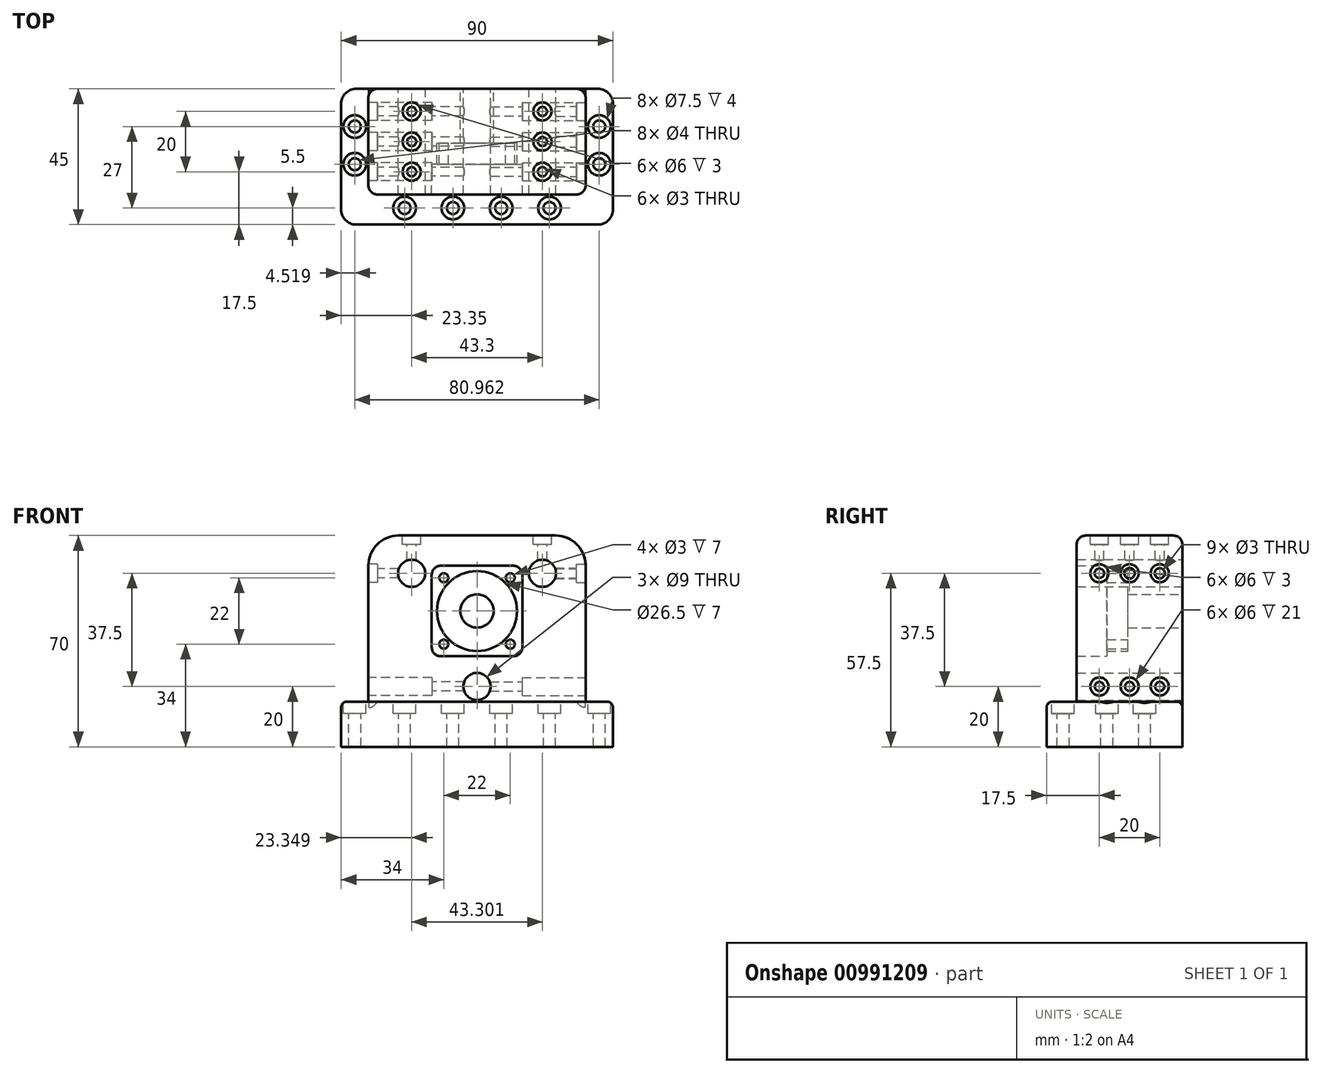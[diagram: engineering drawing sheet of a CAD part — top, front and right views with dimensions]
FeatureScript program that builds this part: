
annotation { "Feature Type Name" : "Feature", "Feature Type Description" : "" }
export const myFeature = defineFeature(function(context is Context, id is Id, definition is map)
    precondition{}
    {
        {
            var Q0;
            Q0=qCreatedBy(makeId("Front.planeOp"),FACE);
            var sketch = newSketch(context, id + "F0", { "sketchPlane" : qUnion([Q0])});
            skCircle(sketch, "E0", {"center": v(0, 0) * mm, "radius": 25 * mm, "construction": true});
            skLineSegment(sketch, "E1.0", {"start": v(0, -25) * mm, "end": v(-21.65, 12.5) * mm, "construction": true});
            skLineSegment(sketch, "E1.1", {"start": v(-21.65, 12.5) * mm, "end": v(21.65, 12.5) * mm, "construction": true});
            skLineSegment(sketch, "E1.2", {"start": v(21.65, 12.5) * mm, "end": v(0, -25) * mm, "construction": true});
            skCircle(sketch, "E2", {"center": v(21.65, 12.5) * mm, "radius": 4.5 * mm});
            skCircle(sketch, "E3", {"center": v(-21.65, 12.5) * mm, "radius": 4.5 * mm});
            skCircle(sketch, "E4", {"center": v(0, -25) * mm, "radius": 4.5 * mm});
            skPoint(sketch, "E5.cCircle.perimeterSnap0", {"position": v(0, 12.5) * mm});
            skLineSegment(sketch, "E5.0", {"start": v(-25.98, 25) * mm, "end": v(25.98, 25) * mm});
            skLineSegment(sketch, "E5.1", {"start": v(34.64, 10) * mm, "end": v(8.66, -35) * mm, "construction": true});
            skLineSegment(sketch, "E5.2", {"start": v(-8.66, -35) * mm, "end": v(-34.64, 10) * mm, "construction": true});
            skPoint(sketch, "E5.0.midPoint.positionSnap0", {"position": v(0, 12.5) * mm});
            skArc(sketch, "E6.filletArc", {"start": v(-25.98, 25) * mm, "mid": v(-34.64, 20) * mm, "end": v(-34.64, 10) * mm});
            skArc(sketch, "E7.filletArc", {"start": v(34.64, 10) * mm, "mid": v(34.64, 20) * mm, "end": v(25.98, 25) * mm});
            skArc(sketch, "E8.filletArc", {"start": v(-8.66, -35) * mm, "mid": v(0, -40) * mm, "end": v(8.66, -35) * mm, "construction": true});
            skLineSegment(sketch, "E9", {"start": v(35.98, 15) * mm, "end": v(35.98, -45) * mm});
            skCircle(sketch, "E10", {"center": v(0, 0) * mm, "radius": 5.5 * mm});
            skLineSegment(sketch, "E11", {"start": v(-35.98, 15) * mm, "end": v(-35.98, -45) * mm});
            skLineSegment(sketch, "E12", {"start": v(-35.98, -45) * mm, "end": v(35.98, -45) * mm});
            skLineSegment(sketch, "E13", {"start": v(-21.65, 12.5) * mm, "end": v(-35.98, 12.5) * mm, "construction": true});
            skLineSegment(sketch, "E14", {"start": v(21.65, 12.5) * mm, "end": v(35.98, 12.5) * mm, "construction": true});
            skLineSegment(sketch, "E15", {"start": v(0, -25) * mm, "end": v(35.98, -25) * mm, "construction": true});
            skLineSegment(sketch, "E16", {"start": v(0, -25) * mm, "end": v(-35.98, -25) * mm, "construction": true});
            skLineSegment(sketch, "E17", {"start": v(21.65, 12.5) * mm, "end": v(21.65, 25) * mm, "construction": true});
            skLineSegment(sketch, "E18", {"start": v(-21.65, 12.5) * mm, "end": v(-21.65, 25) * mm, "construction": true});
            skSolve(sketch);
        }
        {
            var Q0;
            Q0=qSketchRegion(id+"F0",true);
            extrude(context, id + "F1", {"entities" : qUnion([Q0]), "depth" : 18 * mm, "offsetDistance" : 25 * mm});
        }
        {
            var Q0;
            Q0=makeQuery(id+"F1.opExtrude","CAP_FACE",FACE,{"disambiguationData":[OSD([sQuery(id+"F0.wireOp",EDGE,"E2"),sQuery(id+"F0.wireOp",EDGE,"E3"),sQuery(id+"F0.wireOp",EDGE,"E4"),sQuery(id+"F0.wireOp",EDGE,"E5.0"),sQuery(id+"F0.wireOp",EDGE,"E6.filletArc"),sQuery(id+"F0.wireOp",EDGE,"E7.filletArc"),sQuery(id+"F0.wireOp",EDGE,"E9"),sQuery(id+"F0.wireOp",EDGE,"E10"),sQuery(id+"F0.wireOp",EDGE,"E11"),sQuery(id+"F0.wireOp",EDGE,"E12")])],"isStart":false});
            var sketch = newSketch(context, id + "F2", { "sketchPlane" : qUnion([Q0])});
            skCircle(sketch, "E19", {"center": v(0, 0) * mm, "radius": 13.25 * mm});
            skPoint(sketch, "E20.0.midPoint", {"position": v(0, 13.25) * mm});
            skLineSegment(sketch, "E21.bottom", {"start": v(11, 11) * mm, "end": v(-11, 11) * mm});
            skLineSegment(sketch, "E21.top", {"start": v(11, -11) * mm, "end": v(-11, -11) * mm});
            skLineSegment(sketch, "E21.left", {"start": v(11, 11) * mm, "end": v(11, -11) * mm});
            skLineSegment(sketch, "E21.right", {"start": v(-11, 11) * mm, "end": v(-11, -11) * mm});
            skCircle(sketch, "E22", {"center": v(11, 11) * mm, "radius": 1.5 * mm});
            skCircle(sketch, "E23", {"center": v(-11, 11) * mm, "radius": 1.5 * mm});
            skCircle(sketch, "E24", {"center": v(-11, -11) * mm, "radius": 1.5 * mm});
            skCircle(sketch, "E25", {"center": v(11, -11) * mm, "radius": 1.5 * mm});
            skSolve(sketch);
        }
        {
            var Q0;
            {var subQ0=sQuery(id+"F2.wireOp",EDGE,"E20.0");var subQ1=sQuery(id+"F2.wireOp",EDGE,"E19");var subQ2=makeQuery(id+"F2.imprint","INTERSECT",VERTEX,{"derivedFrom":[subQ1,subQ0]});Q0=makeQuery(id+"F2.imprint","IMPRINT",FACE,{"disambiguationData":[TD([[makeQuery(id+"F2.imprint","IMPRINT",EDGE,{"disambiguationData":[TD([[subQ2,1.0]])],"derivedFrom":subQ1}),-1.0]])]});}
            var Q1;
            {var subQ0=sQuery(id+"F2.wireOp",EDGE,"E20.0");var subQ1=sQuery(id+"F2.wireOp",EDGE,"E19");var subQ2=makeQuery(id+"F2.imprint","INTERSECT",VERTEX,{"derivedFrom":[subQ1,subQ0]});Q1=makeQuery(id+"F2.imprint","IMPRINT",FACE,{"disambiguationData":[TD([[makeQuery(id+"F2.imprint","IMPRINT",EDGE,{"disambiguationData":[TD([[subQ2,-1.0]])],"derivedFrom":subQ1}),-1.0]])]});}
            var Q2;
            {var subQ0=sQuery(id+"F2.wireOp",EDGE,"E20.3");var subQ1=sQuery(id+"F2.wireOp",EDGE,"E19");var subQ2=makeQuery(id+"F2.imprint","INTERSECT",VERTEX,{"derivedFrom":[subQ1,subQ0]});Q2=makeQuery(id+"F2.imprint","IMPRINT",FACE,{"disambiguationData":[TD([[makeQuery(id+"F2.imprint","IMPRINT",EDGE,{"disambiguationData":[TD([[subQ2,-1.0]])],"derivedFrom":subQ1}),-1.0]])]});}
            var Q3;
            {var subQ0=sQuery(id+"F2.wireOp",EDGE,"E20.1");var subQ1=sQuery(id+"F2.wireOp",EDGE,"E19");var subQ2=makeQuery(id+"F2.imprint","INTERSECT",VERTEX,{"derivedFrom":[subQ1,subQ0]});Q3=makeQuery(id+"F2.imprint","IMPRINT",FACE,{"disambiguationData":[TD([[makeQuery(id+"F2.imprint","IMPRINT",EDGE,{"disambiguationData":[TD([[subQ2,1.0]])],"derivedFrom":subQ1}),-1.0]])]});}
            var Q4;
            Q4=makeQuery(id+"F2.imprint","IMPRINT",FACE,{"disambiguationData":[TD([[makeQuery(id+"F2.imprint","IMPRINT",EDGE,{"derivedFrom":makeQuery(id+"F1.opExtrude","CAP_EDGE",EDGE,{"disambiguationData":[OSD([sQuery(id+"F0.wireOp",EDGE,"E2")])],"isStart":false})}),-1.0]])]});
            var Q5;
            {var subQ0=sQuery(id+"F2.wireOp",EDGE,"E21.bottom");var subQ1=sQuery(id+"F2.wireOp",EDGE,"E19");var subQ2=makeQuery(id+"F2.imprint","INTERSECT",VERTEX,{"disambiguationData":[OD(1.0)],"derivedFrom":[subQ1,subQ0]});Q5=makeQuery(id+"F2.imprint","IMPRINT",FACE,{"disambiguationData":[TD([[makeQuery(id+"F2.imprint","IMPRINT",EDGE,{"disambiguationData":[TD([[subQ2,-1.0]])],"derivedFrom":subQ1}),-1.0]])]});}
            var Q6;
            {var subQ0=sQuery(id+"F2.wireOp",EDGE,"E21.bottom");var subQ1=sQuery(id+"F2.wireOp",EDGE,"E19");var subQ2=makeQuery(id+"F2.imprint","INTERSECT",VERTEX,{"disambiguationData":[OD(0.0)],"derivedFrom":[subQ1,subQ0]});Q6=makeQuery(id+"F2.imprint","IMPRINT",FACE,{"disambiguationData":[TD([[makeQuery(id+"F2.imprint","IMPRINT",EDGE,{"disambiguationData":[TD([[subQ2,1.0]])],"derivedFrom":subQ1}),-1.0]])]});}
            var Q7;
            {var subQ0=sQuery(id+"F2.wireOp",EDGE,"E21.top");var subQ1=sQuery(id+"F2.wireOp",EDGE,"E19");var subQ2=makeQuery(id+"F2.imprint","INTERSECT",VERTEX,{"disambiguationData":[OD(1.0)],"derivedFrom":[subQ1,subQ0]});Q7=makeQuery(id+"F2.imprint","IMPRINT",FACE,{"disambiguationData":[TD([[makeQuery(id+"F2.imprint","IMPRINT",EDGE,{"disambiguationData":[TD([[subQ2,-1.0]])],"derivedFrom":subQ1}),-1.0]])]});}
            var Q8;
            {var subQ0=sQuery(id+"F2.wireOp",EDGE,"E21.right");var subQ1=sQuery(id+"F2.wireOp",EDGE,"E19");var subQ2=makeQuery(id+"F2.imprint","INTERSECT",VERTEX,{"disambiguationData":[OD(1.0)],"derivedFrom":[subQ1,subQ0]});Q8=makeQuery(id+"F2.imprint","IMPRINT",FACE,{"disambiguationData":[TD([[makeQuery(id+"F2.imprint","IMPRINT",EDGE,{"disambiguationData":[TD([[subQ2,-1.0]])],"derivedFrom":subQ1}),-1.0]])]});}
            extrude(context, id + "F3", {"entities" : qUnion([Q0, Q1, Q2, Q3, Q4, Q5, Q6, Q7, Q8]), "operationType" : NewBodyOperationType.ADD, "depth" : 7 * mm, "offsetDistance" : 25 * mm});
        }
        {
            var Q0;
            Q0=makeQuery(id+"F3.opExtrude","CAP_FACE",FACE,{"disambiguationData":[OSD([sQuery(id+"F0.wireOp",EDGE,"E2"),sQuery(id+"F0.wireOp",EDGE,"E3"),sQuery(id+"F0.wireOp",EDGE,"E4"),sQuery(id+"F0.wireOp",EDGE,"E5.0"),sQuery(id+"F0.wireOp",EDGE,"E6.filletArc"),sQuery(id+"F0.wireOp",EDGE,"E7.filletArc"),sQuery(id+"F0.wireOp",EDGE,"E9"),sQuery(id+"F0.wireOp",EDGE,"E11"),sQuery(id+"F0.wireOp",EDGE,"E12"),sQuery(id+"F2.wireOp",EDGE,"E19"),sQuery(id+"F2.wireOp",EDGE,"eFj7zF5P-7EVq-kD0F-ThRH-6Hop9WIGIFQv"),sQuery(id+"F2.wireOp",EDGE,"omm04afh-Djjw-QQMO-E9Vr-uDkzuJGtbU2r"),sQuery(id+"F2.wireOp",EDGE,"DAAaBMiw-Czrf-eRyD-MXHk-odGZbSsKrrbm"),sQuery(id+"F2.wireOp",EDGE,"t53pX8GN-pWrL-uYky-B8yh-KqMqTwP7CCYq")])],"isStart":false});
            var sketch = newSketch(context, id + "F4", { "sketchPlane" : qUnion([Q0])});
            skLineSegment(sketch, "E26.bottom", {"start": v(-12, 15) * mm, "end": v(12, 15) * mm});
            skLineSegment(sketch, "E26.top", {"start": v(-12, -15) * mm, "end": v(12, -15) * mm});
            skLineSegment(sketch, "E26.left", {"start": v(-15, 12) * mm, "end": v(-15, -12) * mm});
            skLineSegment(sketch, "E26.right", {"start": v(15, 12) * mm, "end": v(15, -12) * mm});
            skPoint(sketch, "E26.middle", {"position": v(0, 0) * mm});
            skPoint(sketch, "E27.visualSharp", {"position": v(-15, 15) * mm});
            skArc(sketch, "E27.filletArc", {"start": v(-12, 15) * mm, "mid": v(-14.12, 14.12) * mm, "end": v(-15, 12) * mm});
            skPoint(sketch, "E28.visualSharp", {"position": v(15, 15) * mm});
            skArc(sketch, "E28.filletArc", {"start": v(15, 12) * mm, "mid": v(14.12, 14.12) * mm, "end": v(12, 15) * mm});
            skPoint(sketch, "E29.visualSharp", {"position": v(-15, -15) * mm});
            skArc(sketch, "E29.filletArc", {"start": v(-15, -12) * mm, "mid": v(-14.12, -14.12) * mm, "end": v(-12, -15) * mm});
            skPoint(sketch, "E30.visualSharp", {"position": v(15, -15) * mm});
            skArc(sketch, "E30.filletArc", {"start": v(12, -15) * mm, "mid": v(14.12, -14.12) * mm, "end": v(15, -12) * mm});
            skSolve(sketch);
        }
        {
            var Q0;
            Q0=makeQuery(id+"F4.imprint","IMPRINT",FACE,{"disambiguationData":[TD([[makeQuery(id+"F4.imprint","IMPRINT",EDGE,{"derivedFrom":sQuery(id+"F4.wireOp",EDGE,"E26.bottom")}),1.0]])]});
            extrude(context, id + "F5", {"entities" : qUnion([Q0]), "operationType" : NewBodyOperationType.ADD, "depth" : 10 * mm, "offsetDistance" : 25 * mm});
        }
        {
            var Q0;
            {var subQ0=sQuery(id+"F0.wireOp",EDGE,"E9");Q0=makeQuery(id+"F5.boolean.opBoolean","MERGE",FACE,{"derivedFrom":[makeQuery(id+"F3.boolean.opBoolean","MERGE",FACE,{"derivedFrom":[makeQuery(id+"F1.opExtrude","SWEPT_FACE",FACE,{"disambiguationData":[OSD([subQ0])]}),makeQuery(id+"F3.opExtrude","SWEPT_FACE",FACE,{"disambiguationData":[OSD([subQ0])]})]}),makeQuery(id+"F5.opExtrude","SWEPT_FACE",FACE,{"disambiguationData":[OSD([subQ0])]})]});}
            var sketch = newSketch(context, id + "F6", { "sketchPlane" : qUnion([Q0])});
            skLineSegment(sketch, "E31", {"start": v(-17.5, 15) * mm, "end": v(-17.5, 0) * mm, "construction": true});
            skLineSegment(sketch, "E32", {"start": v(-27.5, 15) * mm, "end": v(-27.5, 0) * mm, "construction": true});
            skLineSegment(sketch, "E33", {"start": v(-7.5, 15) * mm, "end": v(-7.5, 0) * mm, "construction": true});
            skLineSegment(sketch, "E34", {"start": v(0, 12.5) * mm, "end": v(-35, 12.5) * mm, "construction": true});
            skCircle(sketch, "E35", {"center": v(-27.5, 12.5) * mm, "radius": 3 * mm});
            skCircle(sketch, "E36", {"center": v(-17.5, 12.5) * mm, "radius": 3 * mm});
            skCircle(sketch, "E37", {"center": v(-7.5, 12.5) * mm, "radius": 3 * mm});
            skCircle(sketch, "E38", {"center": v(-27.5, 12.5) * mm, "radius": 1.57 * mm});
            skCircle(sketch, "E39", {"center": v(-17.5, 12.5) * mm, "radius": 1.74 * mm});
            skCircle(sketch, "E40", {"center": v(-7.5, 12.5) * mm, "radius": 1.68 * mm});
            skLineSegment(sketch, "E41", {"start": v(-27.5, 0) * mm, "end": v(-27.5, -45) * mm, "construction": true});
            skLineSegment(sketch, "E42", {"start": v(-17.5, 0) * mm, "end": v(-17.5, -45) * mm, "construction": true});
            skLineSegment(sketch, "E43", {"start": v(-7.5, 0) * mm, "end": v(-7.5, -45) * mm, "construction": true});
            skLineSegment(sketch, "E44", {"start": v(0, -25) * mm, "end": v(-35, -25) * mm, "construction": true});
            skCircle(sketch, "E45", {"center": v(-27.5, -25) * mm, "radius": 3 * mm});
            skCircle(sketch, "E46", {"center": v(-17.5, -25) * mm, "radius": 3 * mm});
            skCircle(sketch, "E47", {"center": v(-7.5, -25) * mm, "radius": 3 * mm});
            skCircle(sketch, "E48", {"center": v(-27.5, -25) * mm, "radius": 1.5 * mm});
            skCircle(sketch, "E49", {"center": v(-17.5, -25) * mm, "radius": 1.5 * mm});
            skCircle(sketch, "E50", {"center": v(-7.5, -25) * mm, "radius": 1.5 * mm});
            skSolve(sketch);
        }
        {
            var Q0;
            Q0=makeQuery(id+"F6.imprint","IMPRINT",FACE,{"disambiguationData":[TD([[makeQuery(id+"F6.imprint","IMPRINT",EDGE,{"derivedFrom":sQuery(id+"F6.wireOp",EDGE,"E38")}),1.0]])]});
            var Q1;
            Q1=makeQuery(id+"F6.imprint","IMPRINT",FACE,{"disambiguationData":[TD([[makeQuery(id+"F6.imprint","IMPRINT",EDGE,{"derivedFrom":sQuery(id+"F6.wireOp",EDGE,"E39")}),1.0]])]});
            var Q2;
            Q2=makeQuery(id+"F6.imprint","IMPRINT",FACE,{"disambiguationData":[TD([[makeQuery(id+"F6.imprint","IMPRINT",EDGE,{"derivedFrom":sQuery(id+"F6.wireOp",EDGE,"E40")}),1.0]])]});
            var Q3;
            {var subQ0=sQuery(id+"F6.wireOp",EDGE,"E35");var subQ1=sQuery(id+"F0.wireOp",EDGE,"E9");var subQ2=sQuery(id+"F0.wireOp",EDGE,"E7.filletArc");var subQ3=makeQuery(id+"F5.boolean.opBoolean","MERGE",EDGE,{"derivedFrom":[makeQuery(id+"F3.boolean.opBoolean","MERGE",EDGE,{"derivedFrom":[makeQuery(id+"F1.opExtrude","SWEPT_EDGE",EDGE,{"disambiguationData":[OSD([subQ2,subQ1])]}),makeQuery(id+"F3.opExtrude","SWEPT_EDGE",EDGE,{"disambiguationData":[OSD([subQ2,subQ1])]})]}),makeQuery(id+"F5.opExtrude","SWEPT_EDGE",EDGE,{"disambiguationData":[OSD([subQ2,subQ1])]})]});var subQ4=makeQuery(id+"F6.imprint","INTERSECT",VERTEX,{"disambiguationData":[OD(0.0)],"derivedFrom":[subQ3,subQ0]});Q3=makeQuery(id+"F6.imprint","IMPRINT",FACE,{"disambiguationData":[TD([[makeQuery(id+"F6.imprint","IMPRINT",EDGE,{"disambiguationData":[TD([[subQ4,1.0]])],"derivedFrom":subQ0}),1.0]])]});}
            var Q4;
            {var subQ0=sQuery(id+"F6.wireOp",EDGE,"E36");var subQ1=sQuery(id+"F0.wireOp",EDGE,"E9");var subQ2=sQuery(id+"F0.wireOp",EDGE,"E7.filletArc");var subQ3=makeQuery(id+"F5.boolean.opBoolean","MERGE",EDGE,{"derivedFrom":[makeQuery(id+"F3.boolean.opBoolean","MERGE",EDGE,{"derivedFrom":[makeQuery(id+"F1.opExtrude","SWEPT_EDGE",EDGE,{"disambiguationData":[OSD([subQ2,subQ1])]}),makeQuery(id+"F3.opExtrude","SWEPT_EDGE",EDGE,{"disambiguationData":[OSD([subQ2,subQ1])]})]}),makeQuery(id+"F5.opExtrude","SWEPT_EDGE",EDGE,{"disambiguationData":[OSD([subQ2,subQ1])]})]});var subQ4=makeQuery(id+"F6.imprint","INTERSECT",VERTEX,{"disambiguationData":[OD(0.0)],"derivedFrom":[subQ3,subQ0]});Q4=makeQuery(id+"F6.imprint","IMPRINT",FACE,{"disambiguationData":[TD([[makeQuery(id+"F6.imprint","IMPRINT",EDGE,{"disambiguationData":[TD([[subQ4,1.0]])],"derivedFrom":subQ0}),1.0]])]});}
            var Q5;
            {var subQ0=sQuery(id+"F6.wireOp",EDGE,"E37");var subQ1=sQuery(id+"F0.wireOp",EDGE,"E9");var subQ2=sQuery(id+"F0.wireOp",EDGE,"E7.filletArc");var subQ3=makeQuery(id+"F5.boolean.opBoolean","MERGE",EDGE,{"derivedFrom":[makeQuery(id+"F3.boolean.opBoolean","MERGE",EDGE,{"derivedFrom":[makeQuery(id+"F1.opExtrude","SWEPT_EDGE",EDGE,{"disambiguationData":[OSD([subQ2,subQ1])]}),makeQuery(id+"F3.opExtrude","SWEPT_EDGE",EDGE,{"disambiguationData":[OSD([subQ2,subQ1])]})]}),makeQuery(id+"F5.opExtrude","SWEPT_EDGE",EDGE,{"disambiguationData":[OSD([subQ2,subQ1])]})]});var subQ4=makeQuery(id+"F6.imprint","INTERSECT",VERTEX,{"disambiguationData":[OD(0.0)],"derivedFrom":[subQ3,subQ0]});Q5=makeQuery(id+"F6.imprint","IMPRINT",FACE,{"disambiguationData":[TD([[makeQuery(id+"F6.imprint","IMPRINT",EDGE,{"disambiguationData":[TD([[subQ4,-1.0]])],"derivedFrom":subQ0}),1.0]])]});}
            var Q6;
            Q6=makeQuery(id+"F6.imprint","IMPRINT",FACE,{"disambiguationData":[TD([[makeQuery(id+"F6.imprint","IMPRINT",EDGE,{"derivedFrom":sQuery(id+"F6.wireOp",EDGE,"E38")}),-1.0]])]});
            var Q7;
            Q7=makeQuery(id+"F6.imprint","IMPRINT",FACE,{"disambiguationData":[TD([[makeQuery(id+"F6.imprint","IMPRINT",EDGE,{"derivedFrom":sQuery(id+"F6.wireOp",EDGE,"E39")}),-1.0]])]});
            var Q8;
            Q8=makeQuery(id+"F6.imprint","IMPRINT",FACE,{"disambiguationData":[TD([[makeQuery(id+"F6.imprint","IMPRINT",EDGE,{"derivedFrom":sQuery(id+"F6.wireOp",EDGE,"E40")}),-1.0]])]});
            extrude(context, id + "F7", {"entities" : qUnion([Q0, Q1, Q2, Q3, Q4, Q5, Q6, Q7, Q8]), "operationType" : NewBodyOperationType.REMOVE, "oppositeDirection" : true, "depth" : 3 * mm, "offsetDistance" : 25 * mm});
        }
        {
            var Q0;
            Q0=makeQuery(id+"F6.imprint","IMPRINT",FACE,{"disambiguationData":[TD([[makeQuery(id+"F6.imprint","IMPRINT",EDGE,{"derivedFrom":sQuery(id+"F6.wireOp",EDGE,"E38")}),1.0]])]});
            var Q1;
            Q1=makeQuery(id+"F6.imprint","IMPRINT",FACE,{"disambiguationData":[TD([[makeQuery(id+"F6.imprint","IMPRINT",EDGE,{"derivedFrom":sQuery(id+"F6.wireOp",EDGE,"E39")}),1.0]])]});
            var Q2;
            Q2=makeQuery(id+"F6.imprint","IMPRINT",FACE,{"disambiguationData":[TD([[makeQuery(id+"F6.imprint","IMPRINT",EDGE,{"derivedFrom":sQuery(id+"F6.wireOp",EDGE,"E40")}),1.0]])]});
            extrude(context, id + "F8", {"entities" : qUnion([Q0, Q1, Q2]), "operationType" : NewBodyOperationType.REMOVE, "oppositeDirection" : true, "depth" : 11 * mm, "offsetDistance" : 25 * mm});
        }
        {
            var Q0;
            {var subQ0=sQuery(id+"F0.wireOp",EDGE,"E11");Q0=makeQuery(id+"F5.boolean.opBoolean","MERGE",FACE,{"derivedFrom":[makeQuery(id+"F3.boolean.opBoolean","MERGE",FACE,{"derivedFrom":[makeQuery(id+"F1.opExtrude","SWEPT_FACE",FACE,{"disambiguationData":[OSD([subQ0])]}),makeQuery(id+"F3.opExtrude","SWEPT_FACE",FACE,{"disambiguationData":[OSD([subQ0])]})]}),makeQuery(id+"F5.opExtrude","SWEPT_FACE",FACE,{"disambiguationData":[OSD([subQ0])]})]});}
            var sketch = newSketch(context, id + "F9", { "sketchPlane" : qUnion([Q0])});
            skLineSegment(sketch, "E51", {"start": v(17.5, 15) * mm, "end": v(17.5, 0) * mm, "construction": true});
            skLineSegment(sketch, "E52", {"start": v(27.5, 15) * mm, "end": v(27.5, 0) * mm, "construction": true});
            skLineSegment(sketch, "E53", {"start": v(7.5, 15) * mm, "end": v(7.5, 0) * mm, "construction": true});
            skLineSegment(sketch, "E54", {"start": v(0, 12.5) * mm, "end": v(35, 12.5) * mm, "construction": true});
            skCircle(sketch, "E55", {"center": v(7.5, 12.5) * mm, "radius": 3 * mm});
            skCircle(sketch, "E56", {"center": v(17.5, 12.5) * mm, "radius": 3 * mm});
            skCircle(sketch, "E57", {"center": v(27.5, 12.5) * mm, "radius": 3 * mm});
            skCircle(sketch, "E58", {"center": v(27.5, 12.5) * mm, "radius": 1.5 * mm});
            skCircle(sketch, "E59", {"center": v(17.5, 12.5) * mm, "radius": 1.5 * mm});
            skCircle(sketch, "E60", {"center": v(7.5, 12.5) * mm, "radius": 1.5 * mm});
            skLineSegment(sketch, "E61", {"start": v(7.5, 0) * mm, "end": v(7.5, -45) * mm, "construction": true});
            skLineSegment(sketch, "E62", {"start": v(17.5, 0) * mm, "end": v(17.5, -45) * mm, "construction": true});
            skLineSegment(sketch, "E63", {"start": v(27.5, 0) * mm, "end": v(27.5, -45) * mm, "construction": true});
            skLineSegment(sketch, "E64", {"start": v(0, -25) * mm, "end": v(35, -25) * mm, "construction": true});
            skCircle(sketch, "E65", {"center": v(7.5, -25) * mm, "radius": 3 * mm});
            skCircle(sketch, "E66", {"center": v(17.5, -25) * mm, "radius": 3 * mm});
            skCircle(sketch, "E67", {"center": v(27.5, -25) * mm, "radius": 3 * mm});
            skCircle(sketch, "E68", {"center": v(7.5, -25) * mm, "radius": 1.5 * mm});
            skCircle(sketch, "E69", {"center": v(17.5, -25) * mm, "radius": 1.5 * mm});
            skCircle(sketch, "E70", {"center": v(27.5, -25) * mm, "radius": 1.5 * mm});
            skSolve(sketch);
        }
        {
            var Q0;
            Q0=makeQuery(id+"F9.imprint","IMPRINT",FACE,{"disambiguationData":[TD([[makeQuery(id+"F9.imprint","IMPRINT",EDGE,{"derivedFrom":sQuery(id+"F9.wireOp",EDGE,"E60")}),-1.0]])]});
            var Q1;
            Q1=makeQuery(id+"F9.imprint","IMPRINT",FACE,{"disambiguationData":[TD([[makeQuery(id+"F9.imprint","IMPRINT",EDGE,{"derivedFrom":sQuery(id+"F9.wireOp",EDGE,"E60")}),1.0]])]});
            var Q2;
            Q2=makeQuery(id+"F9.imprint","IMPRINT",FACE,{"disambiguationData":[TD([[makeQuery(id+"F9.imprint","IMPRINT",EDGE,{"derivedFrom":sQuery(id+"F9.wireOp",EDGE,"E59")}),-1.0]])]});
            var Q3;
            {var subQ0=sQuery(id+"F9.wireOp",EDGE,"E56");var subQ1=sQuery(id+"F0.wireOp",EDGE,"E11");var subQ2=sQuery(id+"F0.wireOp",EDGE,"E6.filletArc");var subQ3=makeQuery(id+"F5.boolean.opBoolean","MERGE",EDGE,{"derivedFrom":[makeQuery(id+"F3.boolean.opBoolean","MERGE",EDGE,{"derivedFrom":[makeQuery(id+"F1.opExtrude","SWEPT_EDGE",EDGE,{"disambiguationData":[OSD([subQ2,subQ1])]}),makeQuery(id+"F3.opExtrude","SWEPT_EDGE",EDGE,{"disambiguationData":[OSD([subQ2,subQ1])]})]}),makeQuery(id+"F5.opExtrude","SWEPT_EDGE",EDGE,{"disambiguationData":[OSD([subQ2,subQ1])]})]});var subQ4=makeQuery(id+"F9.imprint","INTERSECT",VERTEX,{"disambiguationData":[OD(0.0)],"derivedFrom":[subQ3,subQ0]});Q3=makeQuery(id+"F9.imprint","IMPRINT",FACE,{"disambiguationData":[TD([[makeQuery(id+"F9.imprint","IMPRINT",EDGE,{"disambiguationData":[TD([[subQ4,1.0]])],"derivedFrom":subQ0}),1.0]])]});}
            var Q4;
            Q4=makeQuery(id+"F9.imprint","IMPRINT",FACE,{"disambiguationData":[TD([[makeQuery(id+"F9.imprint","IMPRINT",EDGE,{"derivedFrom":sQuery(id+"F9.wireOp",EDGE,"E59")}),1.0]])]});
            var Q5;
            Q5=makeQuery(id+"F9.imprint","IMPRINT",FACE,{"disambiguationData":[TD([[makeQuery(id+"F9.imprint","IMPRINT",EDGE,{"derivedFrom":sQuery(id+"F9.wireOp",EDGE,"E58")}),-1.0]])]});
            var Q6;
            {var subQ0=sQuery(id+"F9.wireOp",EDGE,"E57");var subQ1=sQuery(id+"F0.wireOp",EDGE,"E11");var subQ2=sQuery(id+"F0.wireOp",EDGE,"E6.filletArc");var subQ3=makeQuery(id+"F5.boolean.opBoolean","MERGE",EDGE,{"derivedFrom":[makeQuery(id+"F3.boolean.opBoolean","MERGE",EDGE,{"derivedFrom":[makeQuery(id+"F1.opExtrude","SWEPT_EDGE",EDGE,{"disambiguationData":[OSD([subQ2,subQ1])]}),makeQuery(id+"F3.opExtrude","SWEPT_EDGE",EDGE,{"disambiguationData":[OSD([subQ2,subQ1])]})]}),makeQuery(id+"F5.opExtrude","SWEPT_EDGE",EDGE,{"disambiguationData":[OSD([subQ2,subQ1])]})]});var subQ4=makeQuery(id+"F9.imprint","INTERSECT",VERTEX,{"disambiguationData":[OD(0.0)],"derivedFrom":[subQ3,subQ0]});Q6=makeQuery(id+"F9.imprint","IMPRINT",FACE,{"disambiguationData":[TD([[makeQuery(id+"F9.imprint","IMPRINT",EDGE,{"disambiguationData":[TD([[subQ4,-1.0]])],"derivedFrom":subQ0}),1.0]])]});}
            var Q7;
            Q7=makeQuery(id+"F9.imprint","IMPRINT",FACE,{"disambiguationData":[TD([[makeQuery(id+"F9.imprint","IMPRINT",EDGE,{"derivedFrom":sQuery(id+"F9.wireOp",EDGE,"E58")}),1.0]])]});
            var Q8;
            {var subQ0=sQuery(id+"F9.wireOp",EDGE,"E55");var subQ1=sQuery(id+"F0.wireOp",EDGE,"E11");var subQ2=sQuery(id+"F0.wireOp",EDGE,"E6.filletArc");var subQ3=makeQuery(id+"F5.boolean.opBoolean","MERGE",EDGE,{"derivedFrom":[makeQuery(id+"F3.boolean.opBoolean","MERGE",EDGE,{"derivedFrom":[makeQuery(id+"F1.opExtrude","SWEPT_EDGE",EDGE,{"disambiguationData":[OSD([subQ2,subQ1])]}),makeQuery(id+"F3.opExtrude","SWEPT_EDGE",EDGE,{"disambiguationData":[OSD([subQ2,subQ1])]})]}),makeQuery(id+"F5.opExtrude","SWEPT_EDGE",EDGE,{"disambiguationData":[OSD([subQ2,subQ1])]})]});var subQ4=makeQuery(id+"F9.imprint","INTERSECT",VERTEX,{"disambiguationData":[OD(0.0)],"derivedFrom":[subQ3,subQ0]});Q8=makeQuery(id+"F9.imprint","IMPRINT",FACE,{"disambiguationData":[TD([[makeQuery(id+"F9.imprint","IMPRINT",EDGE,{"disambiguationData":[TD([[subQ4,1.0]])],"derivedFrom":subQ0}),1.0]])]});}
            extrude(context, id + "F10", {"entities" : qUnion([Q0, Q1, Q2, Q3, Q4, Q5, Q6, Q7, Q8]), "operationType" : NewBodyOperationType.REMOVE, "oppositeDirection" : true, "depth" : 3 * mm, "offsetDistance" : 25 * mm});
        }
        {
            var Q0;
            Q0=makeQuery(id+"F9.imprint","IMPRINT",FACE,{"disambiguationData":[TD([[makeQuery(id+"F9.imprint","IMPRINT",EDGE,{"derivedFrom":sQuery(id+"F9.wireOp",EDGE,"E60")}),1.0]])]});
            var Q1;
            Q1=makeQuery(id+"F9.imprint","IMPRINT",FACE,{"disambiguationData":[TD([[makeQuery(id+"F9.imprint","IMPRINT",EDGE,{"derivedFrom":sQuery(id+"F9.wireOp",EDGE,"E59")}),1.0]])]});
            var Q2;
            Q2=makeQuery(id+"F9.imprint","IMPRINT",FACE,{"disambiguationData":[TD([[makeQuery(id+"F9.imprint","IMPRINT",EDGE,{"derivedFrom":sQuery(id+"F9.wireOp",EDGE,"E58")}),1.0]])]});
            extrude(context, id + "F11", {"entities" : qUnion([Q0, Q1, Q2]), "operationType" : NewBodyOperationType.REMOVE, "oppositeDirection" : true, "depth" : 11 * mm, "offsetDistance" : 25 * mm});
        }
        {
            var Q0;
            {var subQ0=sQuery(id+"F0.wireOp",EDGE,"E5.0");Q0=makeQuery(id+"F5.boolean.opBoolean","MERGE",FACE,{"derivedFrom":[makeQuery(id+"F3.boolean.opBoolean","MERGE",FACE,{"derivedFrom":[makeQuery(id+"F1.opExtrude","SWEPT_FACE",FACE,{"disambiguationData":[OSD([subQ0])]}),makeQuery(id+"F3.opExtrude","SWEPT_FACE",FACE,{"disambiguationData":[OSD([subQ0])]})]}),makeQuery(id+"F5.opExtrude","SWEPT_FACE",FACE,{"disambiguationData":[OSD([subQ0])]})]});}
            var sketch = newSketch(context, id + "F12", { "sketchPlane" : qUnion([Q0])});
            skLineSegment(sketch, "E71", {"start": v(-25.98, -17.5) * mm, "end": v(25.98, -17.5) * mm, "construction": true});
            skLineSegment(sketch, "E72", {"start": v(25.98, -7.5) * mm, "end": v(-25.98, -7.5) * mm, "construction": true});
            skLineSegment(sketch, "E73", {"start": v(25.98, -27.5) * mm, "end": v(-25.98, -27.5) * mm, "construction": true});
            skLineSegment(sketch, "E74", {"start": v(-21.65, 0) * mm, "end": v(-21.65, -35) * mm, "construction": true});
            skLineSegment(sketch, "E75", {"start": v(21.65, 0) * mm, "end": v(21.65, -35) * mm, "construction": true});
            skCircle(sketch, "E76", {"center": v(-21.65, -7.5) * mm, "radius": 3 * mm});
            skCircle(sketch, "E77", {"center": v(-21.65, -17.5) * mm, "radius": 3 * mm});
            skCircle(sketch, "E78", {"center": v(-21.65, -27.5) * mm, "radius": 3 * mm});
            skCircle(sketch, "E79", {"center": v(21.65, -7.5) * mm, "radius": 3 * mm});
            skCircle(sketch, "E80", {"center": v(21.65, -17.5) * mm, "radius": 3 * mm});
            skCircle(sketch, "E81", {"center": v(21.65, -27.5) * mm, "radius": 3 * mm});
            skCircle(sketch, "E82", {"center": v(-21.65, -7.5) * mm, "radius": 1.5 * mm});
            skCircle(sketch, "E83", {"center": v(-21.65, -17.5) * mm, "radius": 1.5 * mm});
            skCircle(sketch, "E84", {"center": v(-21.65, -27.5) * mm, "radius": 1.5 * mm});
            skCircle(sketch, "E85", {"center": v(21.65, -7.5) * mm, "radius": 1.5 * mm});
            skCircle(sketch, "E86", {"center": v(21.65, -17.5) * mm, "radius": 1.5 * mm});
            skCircle(sketch, "E87", {"center": v(21.65, -27.5) * mm, "radius": 1.5 * mm});
            skSolve(sketch);
        }
        {
            var Q0;
            Q0=makeQuery(id+"F12.imprint","IMPRINT",FACE,{"disambiguationData":[TD([[makeQuery(id+"F12.imprint","IMPRINT",EDGE,{"derivedFrom":sQuery(id+"F12.wireOp",EDGE,"E76")}),1.0]])]});
            var Q1;
            Q1=makeQuery(id+"F12.imprint","IMPRINT",FACE,{"disambiguationData":[TD([[makeQuery(id+"F12.imprint","IMPRINT",EDGE,{"derivedFrom":sQuery(id+"F12.wireOp",EDGE,"E77")}),1.0]])]});
            var Q2;
            Q2=makeQuery(id+"F12.imprint","IMPRINT",FACE,{"disambiguationData":[TD([[makeQuery(id+"F12.imprint","IMPRINT",EDGE,{"derivedFrom":sQuery(id+"F12.wireOp",EDGE,"E78")}),1.0]])]});
            var Q3;
            Q3=makeQuery(id+"F12.imprint","IMPRINT",FACE,{"disambiguationData":[TD([[makeQuery(id+"F12.imprint","IMPRINT",EDGE,{"derivedFrom":sQuery(id+"F12.wireOp",EDGE,"E79")}),1.0]])]});
            var Q4;
            Q4=makeQuery(id+"F12.imprint","IMPRINT",FACE,{"disambiguationData":[TD([[makeQuery(id+"F12.imprint","IMPRINT",EDGE,{"derivedFrom":sQuery(id+"F12.wireOp",EDGE,"E80")}),1.0]])]});
            var Q5;
            Q5=makeQuery(id+"F12.imprint","IMPRINT",FACE,{"disambiguationData":[TD([[makeQuery(id+"F12.imprint","IMPRINT",EDGE,{"derivedFrom":sQuery(id+"F12.wireOp",EDGE,"E81")}),1.0]])]});
            extrude(context, id + "F13", {"entities" : qUnion([Q0, Q1, Q2, Q3, Q4, Q5]), "operationType" : NewBodyOperationType.REMOVE, "oppositeDirection" : true, "depth" : 3 * mm, "offsetDistance" : 25 * mm});
        }
        {
            var Q0;
            Q0=makeQuery(id+"F12.imprint","IMPRINT",FACE,{"disambiguationData":[TD([[makeQuery(id+"F12.imprint","IMPRINT",EDGE,{"derivedFrom":sQuery(id+"F12.wireOp",EDGE,"E82")}),1.0]])]});
            var Q1;
            Q1=makeQuery(id+"F12.imprint","IMPRINT",FACE,{"disambiguationData":[TD([[makeQuery(id+"F12.imprint","IMPRINT",EDGE,{"derivedFrom":sQuery(id+"F12.wireOp",EDGE,"E83")}),1.0]])]});
            var Q2;
            Q2=makeQuery(id+"F12.imprint","IMPRINT",FACE,{"disambiguationData":[TD([[makeQuery(id+"F12.imprint","IMPRINT",EDGE,{"derivedFrom":sQuery(id+"F12.wireOp",EDGE,"E84")}),1.0]])]});
            var Q3;
            Q3=makeQuery(id+"F12.imprint","IMPRINT",FACE,{"disambiguationData":[TD([[makeQuery(id+"F12.imprint","IMPRINT",EDGE,{"derivedFrom":sQuery(id+"F12.wireOp",EDGE,"E85")}),1.0]])]});
            var Q4;
            Q4=makeQuery(id+"F12.imprint","IMPRINT",FACE,{"disambiguationData":[TD([[makeQuery(id+"F12.imprint","IMPRINT",EDGE,{"derivedFrom":sQuery(id+"F12.wireOp",EDGE,"E86")}),1.0]])]});
            var Q5;
            Q5=makeQuery(id+"F12.imprint","IMPRINT",FACE,{"disambiguationData":[TD([[makeQuery(id+"F12.imprint","IMPRINT",EDGE,{"derivedFrom":sQuery(id+"F12.wireOp",EDGE,"E87")}),1.0]])]});
            extrude(context, id + "F14", {"entities" : qUnion([Q0, Q1, Q2, Q3, Q4, Q5]), "operationType" : NewBodyOperationType.REMOVE, "oppositeDirection" : true, "depth" : 11 * mm, "offsetDistance" : 25 * mm});
        }
        {
            var Q0;
            Q0=makeQuery(id+"F5.opExtrude","CAP_EDGE",EDGE,{"disambiguationData":[OSD([sQuery(id+"F0.wireOp",EDGE,"E5.0")])],"isStart":false});
            fillet(context, id + "F15", {"entities" : qUnion([Q0]), "radius" : 3 * mm, "tangentPropagation" : true, "allowEdgeOverflow" : false});
        }
        {
            var Q0;
            Q0=makeQuery(id+"F1.opExtrude","CAP_EDGE",EDGE,{"disambiguationData":[OSD([sQuery(id+"F0.wireOp",EDGE,"E5.0")])],"isStart":true});
            fillet(context, id + "F16", {"entities" : qUnion([Q0]), "radius" : 3 * mm, "tangentPropagation" : true, "allowEdgeOverflow" : false});
        }
        {
            var Q0;
            Q0=makeQuery(id+"F6.imprint","IMPRINT",FACE,{"disambiguationData":[TD([[makeQuery(id+"F6.imprint","IMPRINT",EDGE,{"derivedFrom":sQuery(id+"F6.wireOp",EDGE,"E45")}),1.0]])]});
            var Q1;
            Q1=makeQuery(id+"F6.imprint","IMPRINT",FACE,{"disambiguationData":[TD([[makeQuery(id+"F6.imprint","IMPRINT",EDGE,{"derivedFrom":sQuery(id+"F6.wireOp",EDGE,"E48")}),1.0]])]});
            var Q2;
            Q2=makeQuery(id+"F6.imprint","IMPRINT",FACE,{"disambiguationData":[TD([[makeQuery(id+"F6.imprint","IMPRINT",EDGE,{"derivedFrom":sQuery(id+"F6.wireOp",EDGE,"E46")}),1.0]])]});
            var Q3;
            Q3=makeQuery(id+"F6.imprint","IMPRINT",FACE,{"disambiguationData":[TD([[makeQuery(id+"F6.imprint","IMPRINT",EDGE,{"derivedFrom":sQuery(id+"F6.wireOp",EDGE,"E49")}),1.0]])]});
            var Q4;
            Q4=makeQuery(id+"F6.imprint","IMPRINT",FACE,{"disambiguationData":[TD([[makeQuery(id+"F6.imprint","IMPRINT",EDGE,{"derivedFrom":sQuery(id+"F6.wireOp",EDGE,"E47")}),1.0]])]});
            var Q5;
            Q5=makeQuery(id+"F6.imprint","IMPRINT",FACE,{"disambiguationData":[TD([[makeQuery(id+"F6.imprint","IMPRINT",EDGE,{"derivedFrom":sQuery(id+"F6.wireOp",EDGE,"E50")}),1.0]])]});
            extrude(context, id + "F17", {"entities" : qUnion([Q0, Q1, Q2, Q3, Q4, Q5]), "operationType" : NewBodyOperationType.REMOVE, "oppositeDirection" : true, "depth" : 21 * mm, "offsetDistance" : 25 * mm});
        }
        {
            var Q0;
            Q0=makeQuery(id+"F6.imprint","IMPRINT",FACE,{"disambiguationData":[TD([[makeQuery(id+"F6.imprint","IMPRINT",EDGE,{"derivedFrom":sQuery(id+"F6.wireOp",EDGE,"E48")}),1.0]])]});
            var Q1;
            Q1=makeQuery(id+"F6.imprint","IMPRINT",FACE,{"disambiguationData":[TD([[makeQuery(id+"F6.imprint","IMPRINT",EDGE,{"derivedFrom":sQuery(id+"F6.wireOp",EDGE,"E49")}),1.0]])]});
            var Q2;
            Q2=makeQuery(id+"F6.imprint","IMPRINT",FACE,{"disambiguationData":[TD([[makeQuery(id+"F6.imprint","IMPRINT",EDGE,{"derivedFrom":sQuery(id+"F6.wireOp",EDGE,"E50")}),1.0]])]});
            extrude(context, id + "F18", {"entities" : qUnion([Q0, Q1, Q2]), "operationType" : NewBodyOperationType.REMOVE, "oppositeDirection" : true, "depth" : 37 * mm, "offsetDistance" : 25 * mm});
        }
        {
            var Q0;
            Q0=makeQuery(id+"F9.imprint","IMPRINT",FACE,{"disambiguationData":[TD([[makeQuery(id+"F9.imprint","IMPRINT",EDGE,{"derivedFrom":sQuery(id+"F9.wireOp",EDGE,"E65")}),1.0]])]});
            var Q1;
            Q1=makeQuery(id+"F9.imprint","IMPRINT",FACE,{"disambiguationData":[TD([[makeQuery(id+"F9.imprint","IMPRINT",EDGE,{"derivedFrom":sQuery(id+"F9.wireOp",EDGE,"E68")}),1.0]])]});
            var Q2;
            Q2=makeQuery(id+"F9.imprint","IMPRINT",FACE,{"disambiguationData":[TD([[makeQuery(id+"F9.imprint","IMPRINT",EDGE,{"derivedFrom":sQuery(id+"F9.wireOp",EDGE,"E66")}),1.0]])]});
            var Q3;
            Q3=makeQuery(id+"F9.imprint","IMPRINT",FACE,{"disambiguationData":[TD([[makeQuery(id+"F9.imprint","IMPRINT",EDGE,{"derivedFrom":sQuery(id+"F9.wireOp",EDGE,"E69")}),1.0]])]});
            var Q4;
            Q4=makeQuery(id+"F9.imprint","IMPRINT",FACE,{"disambiguationData":[TD([[makeQuery(id+"F9.imprint","IMPRINT",EDGE,{"derivedFrom":sQuery(id+"F9.wireOp",EDGE,"E70")}),1.0]])]});
            var Q5;
            Q5=makeQuery(id+"F9.imprint","IMPRINT",FACE,{"disambiguationData":[TD([[makeQuery(id+"F9.imprint","IMPRINT",EDGE,{"derivedFrom":sQuery(id+"F9.wireOp",EDGE,"E67")}),1.0]])]});
            extrude(context, id + "F19", {"entities" : qUnion([Q0, Q1, Q2, Q3, Q4, Q5]), "operationType" : NewBodyOperationType.REMOVE, "oppositeDirection" : true, "depth" : 21 * mm, "offsetDistance" : 25 * mm});
        }
        {
            var Q0;
            Q0=makeQuery(id+"F9.imprint","IMPRINT",FACE,{"disambiguationData":[TD([[makeQuery(id+"F9.imprint","IMPRINT",EDGE,{"derivedFrom":sQuery(id+"F9.wireOp",EDGE,"E68")}),1.0]])]});
            var Q1;
            Q1=makeQuery(id+"F9.imprint","IMPRINT",FACE,{"disambiguationData":[TD([[makeQuery(id+"F9.imprint","IMPRINT",EDGE,{"derivedFrom":sQuery(id+"F9.wireOp",EDGE,"E69")}),1.0]])]});
            var Q2;
            Q2=makeQuery(id+"F9.imprint","IMPRINT",FACE,{"disambiguationData":[TD([[makeQuery(id+"F9.imprint","IMPRINT",EDGE,{"derivedFrom":sQuery(id+"F9.wireOp",EDGE,"E70")}),1.0]])]});
            extrude(context, id + "F20", {"entities" : qUnion([Q0, Q1, Q2]), "operationType" : NewBodyOperationType.REMOVE, "oppositeDirection" : true, "depth" : 37 * mm, "offsetDistance" : 25 * mm});
        }
        {
            var Q0;
            {var subQ0=sQuery(id+"F0.wireOp",EDGE,"E12");Q0=makeQuery(id+"F5.boolean.opBoolean","MERGE",FACE,{"derivedFrom":[makeQuery(id+"F3.boolean.opBoolean","MERGE",FACE,{"derivedFrom":[makeQuery(id+"F1.opExtrude","SWEPT_FACE",FACE,{"disambiguationData":[OSD([subQ0])]}),makeQuery(id+"F3.opExtrude","SWEPT_FACE",FACE,{"disambiguationData":[OSD([subQ0])]})]}),makeQuery(id+"F5.opExtrude","SWEPT_FACE",FACE,{"disambiguationData":[OSD([subQ0])]})]});}
            var sketch = newSketch(context, id + "F21", { "sketchPlane" : qUnion([Q0])});
            skLineSegment(sketch, "E88", {"start": v(32.98, 0) * mm, "end": v(40, 0) * mm});
            skLineSegment(sketch, "E89", {"start": v(45, 5) * mm, "end": v(45, 30) * mm});
            skLineSegment(sketch, "E90", {"start": v(-32.98, 0) * mm, "end": v(-40, 0) * mm});
            skLineSegment(sketch, "E91", {"start": v(-45, 5) * mm, "end": v(-45, 30) * mm});
            skPoint(sketch, "E92.visualSharp", {"position": v(45, 0) * mm});
            skArc(sketch, "E92.filletArc", {"start": v(40, 0) * mm, "mid": v(43.54, 1.46) * mm, "end": v(45, 5) * mm});
            skPoint(sketch, "E93.visualSharp", {"position": v(-45, 0) * mm});
            skArc(sketch, "E93.filletArc", {"start": v(-45, 5) * mm, "mid": v(-43.54, 1.46) * mm, "end": v(-40, 0) * mm});
            skLineSegment(sketch, "E94", {"start": v(-40, 45) * mm, "end": v(40, 45) * mm});
            skLineSegment(sketch, "E95", {"start": v(45, 30) * mm, "end": v(45, 40) * mm});
            skLineSegment(sketch, "E96", {"start": v(-45, 30) * mm, "end": v(-45, 40) * mm});
            skPoint(sketch, "E97.visualSharp", {"position": v(-45, 45) * mm});
            skArc(sketch, "E97.filletArc", {"start": v(-40, 45) * mm, "mid": v(-43.54, 43.54) * mm, "end": v(-45, 40) * mm});
            skPoint(sketch, "E98.visualSharp", {"position": v(45, 45) * mm});
            skArc(sketch, "E98.filletArc", {"start": v(45, 40) * mm, "mid": v(43.54, 43.54) * mm, "end": v(40, 45) * mm});
            skSolve(sketch);
        }
        {
            var Q0;
            Q0=makeQuery(id+"F21.imprint","IMPRINT",FACE,{"disambiguationData":[TD([[makeQuery(id+"F21.imprint","IMPRINT",EDGE,{"derivedFrom":sQuery(id+"F21.wireOp",EDGE,"E88")}),1.0]])]});
            var Q1;
            Q1=makeQuery(id+"F21.imprint","IMPRINT",FACE,{"disambiguationData":[TD([[makeQuery(id+"F21.imprint","IMPRINT",EDGE,{"derivedFrom":sQuery(id+"F21.wireOp",EDGE,"E90")}),-1.0]])]});
            extrude(context, id + "F22", {"entities" : qUnion([Q0, Q1]), "operationType" : NewBodyOperationType.ADD, "oppositeDirection" : true, "depth" : 15 * mm, "offsetDistance" : 25 * mm});
        }
        {
            var Q0;
            Q0=makeQuery(id+"F22.opExtrude","CAP_FACE",FACE,{"disambiguationData":[OSD([sQuery(id+"F0.wireOp",EDGE,"E9"),sQuery(id+"F0.wireOp",EDGE,"E11"),sQuery(id+"F0.wireOp",EDGE,"E12"),sQuery(id+"F21.wireOp",EDGE,"E88"),sQuery(id+"F21.wireOp",EDGE,"E89"),sQuery(id+"F21.wireOp",EDGE,"E90"),sQuery(id+"F21.wireOp",EDGE,"E91"),sQuery(id+"F21.wireOp",EDGE,"E92.filletArc"),sQuery(id+"F21.wireOp",EDGE,"E93.filletArc"),sQuery(id+"F21.wireOp",EDGE,"E94"),sQuery(id+"F21.wireOp",EDGE,"E95"),sQuery(id+"F21.wireOp",EDGE,"E96"),sQuery(id+"F21.wireOp",EDGE,"E97.filletArc"),sQuery(id+"F21.wireOp",EDGE,"E98.filletArc")])],"isStart":false});
            var sketch = newSketch(context, id + "F23", { "sketchPlane" : qUnion([Q0])});
            skCircle(sketch, "E99", {"center": v(-24, -39.5) * mm, "radius": 3.75 * mm});
            skCircle(sketch, "E100", {"center": v(-8, -39.5) * mm, "radius": 3.75 * mm});
            skCircle(sketch, "E101", {"center": v(8, -39.5) * mm, "radius": 3.75 * mm});
            skCircle(sketch, "E102", {"center": v(24, -39.5) * mm, "radius": 3.75 * mm});
            skCircle(sketch, "E103", {"center": v(-24, -39.5) * mm, "radius": 2 * mm});
            skCircle(sketch, "E104", {"center": v(-8, -39.5) * mm, "radius": 2 * mm});
            skCircle(sketch, "E105", {"center": v(8, -39.5) * mm, "radius": 2 * mm});
            skCircle(sketch, "E106", {"center": v(24, -39.5) * mm, "radius": 2 * mm});
            skLineSegment(sketch, "E107", {"start": v(-40, -39.5) * mm, "end": v(40, -39.5) * mm, "construction": true});
            skCircle(sketch, "E108", {"center": v(40.48, -12.5) * mm, "radius": 3.75 * mm});
            skCircle(sketch, "E109", {"center": v(40.48, -12.5) * mm, "radius": 2 * mm});
            skCircle(sketch, "E110", {"center": v(40.48, -25) * mm, "radius": 3.75 * mm});
            skCircle(sketch, "E111", {"center": v(40.48, -25) * mm, "radius": 2 * mm});
            skCircle(sketch, "E112", {"center": v(-40.48, -12.5) * mm, "radius": 3.75 * mm});
            skCircle(sketch, "E113", {"center": v(-40.48, -12.5) * mm, "radius": 2 * mm});
            skCircle(sketch, "E114", {"center": v(-40.48, -25) * mm, "radius": 3.75 * mm});
            skCircle(sketch, "E115", {"center": v(-40.48, -25) * mm, "radius": 2 * mm});
            skLineSegment(sketch, "E116", {"start": v(-40.48, 0) * mm, "end": v(-40.48, -45) * mm, "construction": true});
            skLineSegment(sketch, "E117", {"start": v(40.48, 0) * mm, "end": v(40.48, -45) * mm, "construction": true});
            skSolve(sketch);
        }
        {
            var Q0;
            Q0=makeQuery(id+"F22.opExtrude","CAP_EDGE",EDGE,{"disambiguationData":[OSD([sQuery(id+"F0.wireOp",EDGE,"E12")])],"isStart":false});
            var Q1;
            Q1=makeQuery(id+"F22.opExtrude","CAP_EDGE",EDGE,{"disambiguationData":[OSD([sQuery(id+"F21.wireOp",EDGE,"E94")])],"isStart":false});
            fillet(context, id + "F24", {"entities" : qUnion([Q0, Q1]), "radius" : 2 * mm, "tangentPropagation" : true, "allowEdgeOverflow" : false});
        }
        {
            var Q0;
            Q0=makeQuery(id+"F23.imprint","IMPRINT",FACE,{"disambiguationData":[TD([[makeQuery(id+"F23.imprint","IMPRINT",EDGE,{"derivedFrom":sQuery(id+"F23.wireOp",EDGE,"E110")}),1.0]])]});
            var Q1;
            Q1=makeQuery(id+"F23.imprint","IMPRINT",FACE,{"disambiguationData":[TD([[makeQuery(id+"F23.imprint","IMPRINT",EDGE,{"derivedFrom":sQuery(id+"F23.wireOp",EDGE,"E108")}),1.0]])]});
            var Q2;
            Q2=makeQuery(id+"F23.imprint","IMPRINT",FACE,{"disambiguationData":[TD([[makeQuery(id+"F23.imprint","IMPRINT",EDGE,{"derivedFrom":sQuery(id+"F23.wireOp",EDGE,"E102")}),1.0]])]});
            var Q3;
            Q3=makeQuery(id+"F23.imprint","IMPRINT",FACE,{"disambiguationData":[TD([[makeQuery(id+"F23.imprint","IMPRINT",EDGE,{"derivedFrom":sQuery(id+"F23.wireOp",EDGE,"E101")}),1.0]])]});
            var Q4;
            Q4=makeQuery(id+"F23.imprint","IMPRINT",FACE,{"disambiguationData":[TD([[makeQuery(id+"F23.imprint","IMPRINT",EDGE,{"derivedFrom":sQuery(id+"F23.wireOp",EDGE,"E100")}),1.0]])]});
            var Q5;
            Q5=makeQuery(id+"F23.imprint","IMPRINT",FACE,{"disambiguationData":[TD([[makeQuery(id+"F23.imprint","IMPRINT",EDGE,{"derivedFrom":sQuery(id+"F23.wireOp",EDGE,"E99")}),1.0]])]});
            var Q6;
            Q6=makeQuery(id+"F23.imprint","IMPRINT",FACE,{"disambiguationData":[TD([[makeQuery(id+"F23.imprint","IMPRINT",EDGE,{"derivedFrom":sQuery(id+"F23.wireOp",EDGE,"E114")}),1.0]])]});
            var Q7;
            Q7=makeQuery(id+"F23.imprint","IMPRINT",FACE,{"disambiguationData":[TD([[makeQuery(id+"F23.imprint","IMPRINT",EDGE,{"derivedFrom":sQuery(id+"F23.wireOp",EDGE,"E112")}),1.0]])]});
            extrude(context, id + "F25", {"entities" : qUnion([Q0, Q1, Q2, Q3, Q4, Q5, Q6, Q7]), "operationType" : NewBodyOperationType.REMOVE, "oppositeDirection" : true, "depth" : 8 * mm, "offsetDistance" : 25 * mm, "symmetric" : true});
        }
        {
            var Q0;
            Q0=makeQuery(id+"F23.imprint","IMPRINT",FACE,{"disambiguationData":[TD([[makeQuery(id+"F23.imprint","IMPRINT",EDGE,{"derivedFrom":sQuery(id+"F23.wireOp",EDGE,"E111")}),1.0]])]});
            var Q1;
            Q1=makeQuery(id+"F23.imprint","IMPRINT",FACE,{"disambiguationData":[TD([[makeQuery(id+"F23.imprint","IMPRINT",EDGE,{"derivedFrom":sQuery(id+"F23.wireOp",EDGE,"E106")}),1.0]])]});
            var Q2;
            Q2=makeQuery(id+"F23.imprint","IMPRINT",FACE,{"disambiguationData":[TD([[makeQuery(id+"F23.imprint","IMPRINT",EDGE,{"derivedFrom":sQuery(id+"F23.wireOp",EDGE,"E105")}),1.0]])]});
            var Q3;
            Q3=makeQuery(id+"F23.imprint","IMPRINT",FACE,{"disambiguationData":[TD([[makeQuery(id+"F23.imprint","IMPRINT",EDGE,{"derivedFrom":sQuery(id+"F23.wireOp",EDGE,"E104")}),1.0]])]});
            var Q4;
            Q4=makeQuery(id+"F23.imprint","IMPRINT",FACE,{"disambiguationData":[TD([[makeQuery(id+"F23.imprint","IMPRINT",EDGE,{"derivedFrom":sQuery(id+"F23.wireOp",EDGE,"E103")}),1.0]])]});
            var Q5;
            Q5=makeQuery(id+"F23.imprint","IMPRINT",FACE,{"disambiguationData":[TD([[makeQuery(id+"F23.imprint","IMPRINT",EDGE,{"derivedFrom":sQuery(id+"F23.wireOp",EDGE,"E115")}),1.0]])]});
            var Q6;
            Q6=makeQuery(id+"F23.imprint","IMPRINT",FACE,{"disambiguationData":[TD([[makeQuery(id+"F23.imprint","IMPRINT",EDGE,{"derivedFrom":sQuery(id+"F23.wireOp",EDGE,"E113")}),1.0]])]});
            var Q7;
            Q7=makeQuery(id+"F23.imprint","IMPRINT",FACE,{"disambiguationData":[TD([[makeQuery(id+"F23.imprint","IMPRINT",EDGE,{"derivedFrom":sQuery(id+"F23.wireOp",EDGE,"E109")}),1.0]])]});
            extrude(context, id + "F26", {"entities" : qUnion([Q0, Q1, Q2, Q3, Q4, Q5, Q6, Q7]), "operationType" : NewBodyOperationType.REMOVE, "oppositeDirection" : true, "depth" : 25 * mm, "offsetDistance" : 25 * mm});
        }
    });
